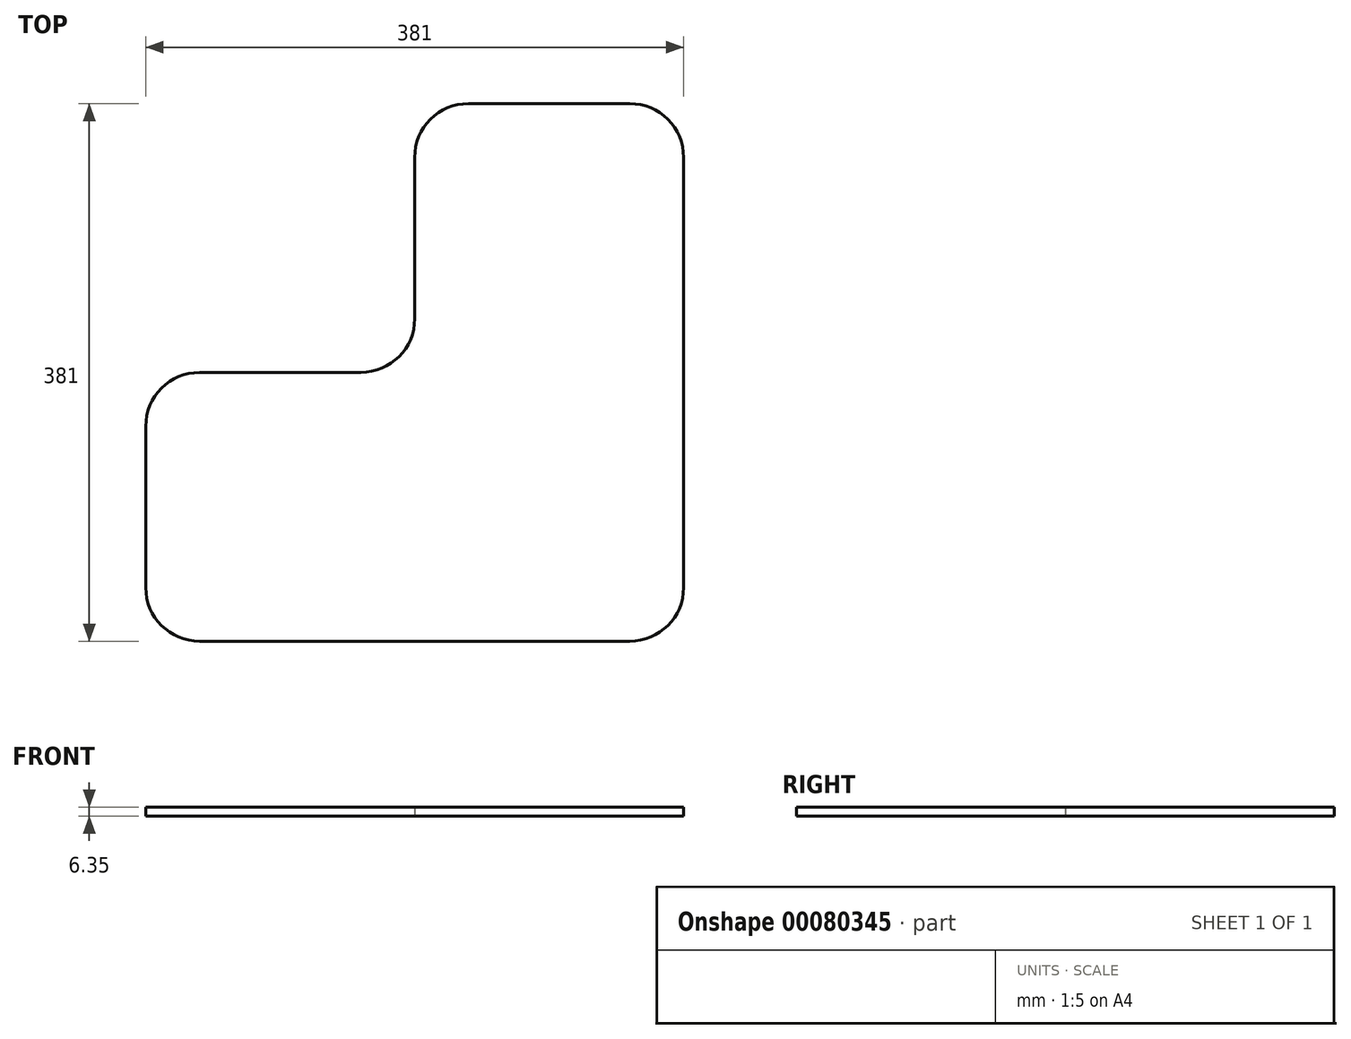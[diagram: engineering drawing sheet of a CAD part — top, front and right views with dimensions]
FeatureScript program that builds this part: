
annotation { "Feature Type Name" : "Feature", "Feature Type Description" : "" }
export const myFeature = defineFeature(function(context is Context, id is Id, definition is map)
    precondition{}
    {
        {
            var Q0;
            Q0=qCreatedBy(makeId("Top.planeOp"),FACE);
            var sketch = newSketch(context, id + "F0", { "sketchPlane" : qUnion([Q0])});
            skLineSegment(sketch, "E0.top", {"start": v(26.66, 128.12) * mm, "end": v(217.16, 128.12) * mm});
            skLineSegment(sketch, "E0.left", {"start": v(26.66, -62.38) * mm, "end": v(26.66, 128.12) * mm});
            skLineSegment(sketch, "E1.bottom", {"start": v(26.66, -62.38) * mm, "end": v(-163.84, -62.38) * mm});
            skLineSegment(sketch, "E1.right", {"start": v(-163.84, -62.38) * mm, "end": v(-163.84, -252.88) * mm});
            skLineSegment(sketch, "E2", {"start": v(217.16, 128.12) * mm, "end": v(217.16, -252.88) * mm});
            skLineSegment(sketch, "E3", {"start": v(-163.84, -252.88) * mm, "end": v(217.16, -252.88) * mm});
            skSolve(sketch);
        }
        {
            var Q0;
            Q0 = qSketchRegion(id + "F0", true);
            extrude(context, id + "F1", {"entities" : qUnion([Q0]), "depth" : 6.35 * mm});
        }
        {
            var Q0;
            Q0=makeQuery(id+"F1.opExtrude","SWEPT_EDGE",EDGE,{"disambiguationData":[OSD([sQuery(id+"F0.wireOp",EDGE,"E2"),sQuery(id+"F0.wireOp",EDGE,"E3")])]});
            var Q1;
            Q1=makeQuery(id+"F1.opExtrude","SWEPT_EDGE",EDGE,{"disambiguationData":[OSD([sQuery(id+"F0.wireOp",EDGE,"E0.top"),sQuery(id+"F0.wireOp",EDGE,"E2")])]});
            var Q2;
            Q2=makeQuery(id+"F1.opExtrude","SWEPT_EDGE",EDGE,{"disambiguationData":[OSD([sQuery(id+"F0.wireOp",EDGE,"E0.top"),sQuery(id+"F0.wireOp",EDGE,"E0.left")])]});
            var Q3;
            Q3=makeQuery(id+"F1.opExtrude","SWEPT_EDGE",EDGE,{"disambiguationData":[OSD([sQuery(id+"F0.wireOp",EDGE,"E0.left"),sQuery(id+"F0.wireOp",EDGE,"E1.bottom")])]});
            var Q4;
            Q4=makeQuery(id+"F1.opExtrude","SWEPT_EDGE",EDGE,{"disambiguationData":[OSD([sQuery(id+"F0.wireOp",EDGE,"E1.bottom"),sQuery(id+"F0.wireOp",EDGE,"E1.right")])]});
            var Q5;
            Q5=makeQuery(id+"F1.opExtrude","SWEPT_EDGE",EDGE,{"disambiguationData":[OSD([sQuery(id+"F0.wireOp",EDGE,"E1.right"),sQuery(id+"F0.wireOp",EDGE,"E3")])]});
            fillet(context, id + "F2", {"entities" : qUnion([Q0, Q1, Q2, Q3, Q4, Q5]), "radius" : 38.1 * mm, "tangentPropagation" : true, "allowEdgeOverflow" : false});
        }
    });
